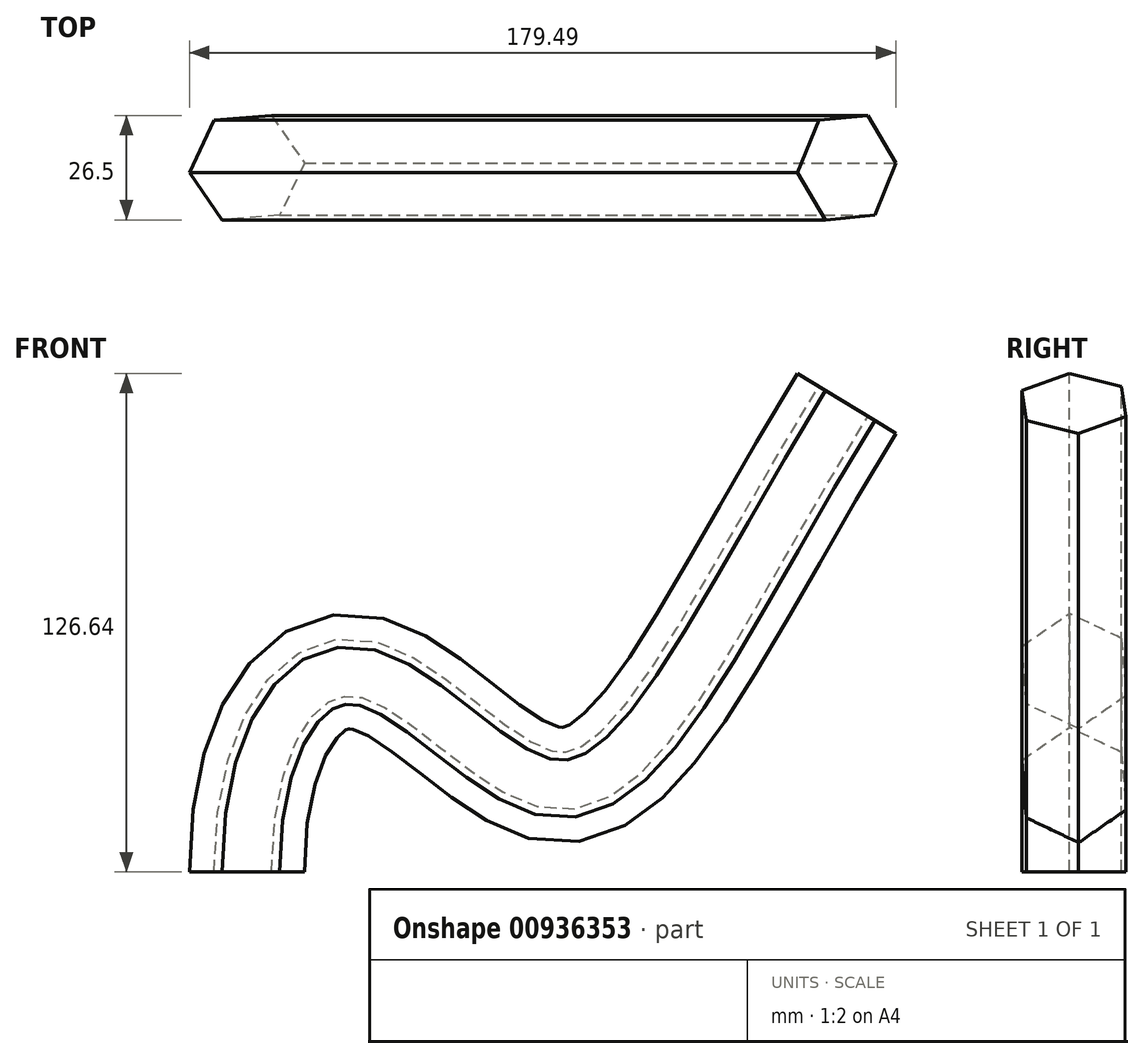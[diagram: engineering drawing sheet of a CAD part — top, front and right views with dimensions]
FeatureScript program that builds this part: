
annotation { "Feature Type Name" : "Feature", "Feature Type Description" : "" }
export const myFeature = defineFeature(function(context is Context, id is Id, definition is map)
    precondition{}
    {
        {
            var Q0;
            Q0=qCreatedBy(makeId("Front.planeOp"),FACE);
            var sketch = newSketch(context, id + "F0", { "sketchPlane" : qUnion([Q0])});
            skFitSpline(sketch, "E0", {"points": [v(0, 0) * mm, v(28.8, 50.8) * mm, v(77.4, 22.25) * mm, v(152.4, 119.01) * mm], "startDerivative": vector(0, 346.46) * mm, "endDerivative": vector(248.24, 405.88) * mm});
            skSolve(sketch);
        }
        {
            var Q0;
            Q0=qCreatedBy(makeId("Top.planeOp"),FACE);
            var sketch = newSketch(context, id + "F1", { "sketchPlane" : qUnion([Q0])});
            skCircle(sketch, "E1.cCircle", {"center": v(0, 0) * mm, "radius": 12.7 * mm, "construction": true});
            skLineSegment(sketch, "E1.0", {"start": v(-6.28, -13.25) * mm, "end": v(-14.62, -1.18) * mm});
            skLineSegment(sketch, "E1.1", {"start": v(-14.62, -1.18) * mm, "end": v(-8.33, 12.07) * mm});
            skLineSegment(sketch, "E1.2", {"start": v(-8.33, 12.07) * mm, "end": v(6.28, 13.25) * mm});
            skLineSegment(sketch, "E1.3", {"start": v(6.28, 13.25) * mm, "end": v(14.62, 1.18) * mm});
            skLineSegment(sketch, "E1.4", {"start": v(14.62, 1.18) * mm, "end": v(8.33, -12.07) * mm});
            skLineSegment(sketch, "E1.5", {"start": v(8.33, -12.07) * mm, "end": v(-6.28, -13.25) * mm});
            skPoint(sketch, "E1.0.midPoint", {"position": v(-10.45, -7.22) * mm});
            skSolve(sketch);
        }
        {
            var Q0;
            Q0 = qSketchRegion(id + "F1", true);
            var Q1;
            Q1=sQuery(id+"F0.wireOp",EDGE,"E0");
            sweep(context, id + "F2", {"profiles" : qUnion([Q0]), "path" : qUnion([Q1])});
        }
    });
